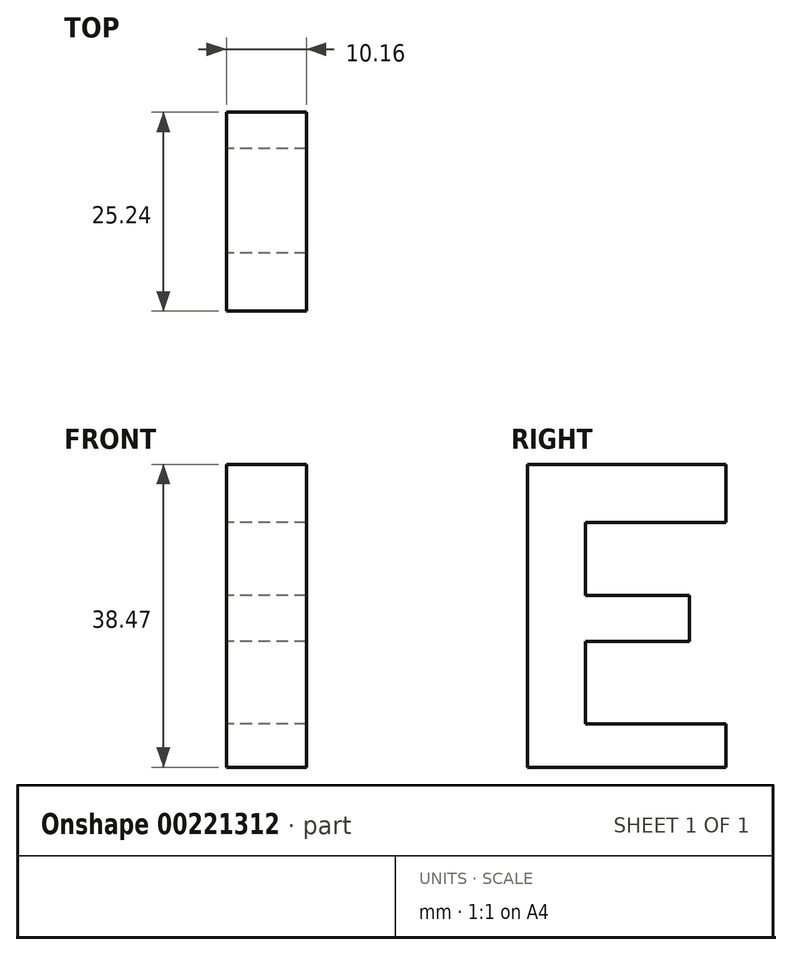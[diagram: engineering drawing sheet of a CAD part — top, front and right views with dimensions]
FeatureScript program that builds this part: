
annotation { "Feature Type Name" : "Feature", "Feature Type Description" : "" }
export const myFeature = defineFeature(function(context is Context, id is Id, definition is map)
    precondition{}
    {
        {
            var Q0;
            Q0=qCreatedBy(makeId("Right.planeOp"),FACE);
            var sketch = newSketch(context, id + "F0", { "sketchPlane" : qUnion([Q0])});
            skLineSegment(sketch, "E0.bottom", {"start": v(0, 25.85) * mm, "end": v(-7.39, 25.85) * mm});
            skLineSegment(sketch, "E0.top", {"start": v(0, -12.62) * mm, "end": v(-7.39, -12.62) * mm});
            skLineSegment(sketch, "E0.right", {"start": v(-7.39, 25.85) * mm, "end": v(-7.39, -12.62) * mm});
            skLineSegment(sketch, "E1.bottom", {"start": v(0, -12.62) * mm, "end": v(17.85, -12.62) * mm});
            skLineSegment(sketch, "E1.top", {"start": v(0, -7.08) * mm, "end": v(17.85, -7.08) * mm});
            skLineSegment(sketch, "E1.right", {"start": v(17.85, -12.62) * mm, "end": v(17.85, -7.08) * mm});
            skLineSegment(sketch, "E2.bottom", {"start": v(0, 3.39) * mm, "end": v(13.23, 3.39) * mm});
            skLineSegment(sketch, "E2.top", {"start": v(0, 9.23) * mm, "end": v(13.23, 9.23) * mm});
            skLineSegment(sketch, "E2.right", {"start": v(13.23, 3.39) * mm, "end": v(13.23, 9.23) * mm});
            skLineSegment(sketch, "E3.bottom", {"start": v(0, 25.85) * mm, "end": v(17.85, 25.85) * mm});
            skLineSegment(sketch, "E3.top", {"start": v(0, 18.46) * mm, "end": v(17.85, 18.46) * mm});
            skLineSegment(sketch, "E3.right", {"start": v(17.85, 25.85) * mm, "end": v(17.85, 18.46) * mm});
            skLineSegment(sketch, "E4", {"start": v(0, 18.46) * mm, "end": v(0, 9.23) * mm});
            skLineSegment(sketch, "E5", {"start": v(0, 3.39) * mm, "end": v(0, -7.08) * mm});
            skSolve(sketch);
        }
        {
            var Q0;
            Q0=makeQuery(id+"F0.imprint","IMPRINT",FACE,{"disambiguationData":[TD([[makeQuery(id+"F0.imprint","IMPRINT",EDGE,{"derivedFrom":sQuery(id+"F0.wireOp",EDGE,"E0.bottom")}),1.0]])]});
            extrude(context, id + "F1", {"entities" : qUnion([Q0]), "depth" : 10.16 * mm});
        }
    });
